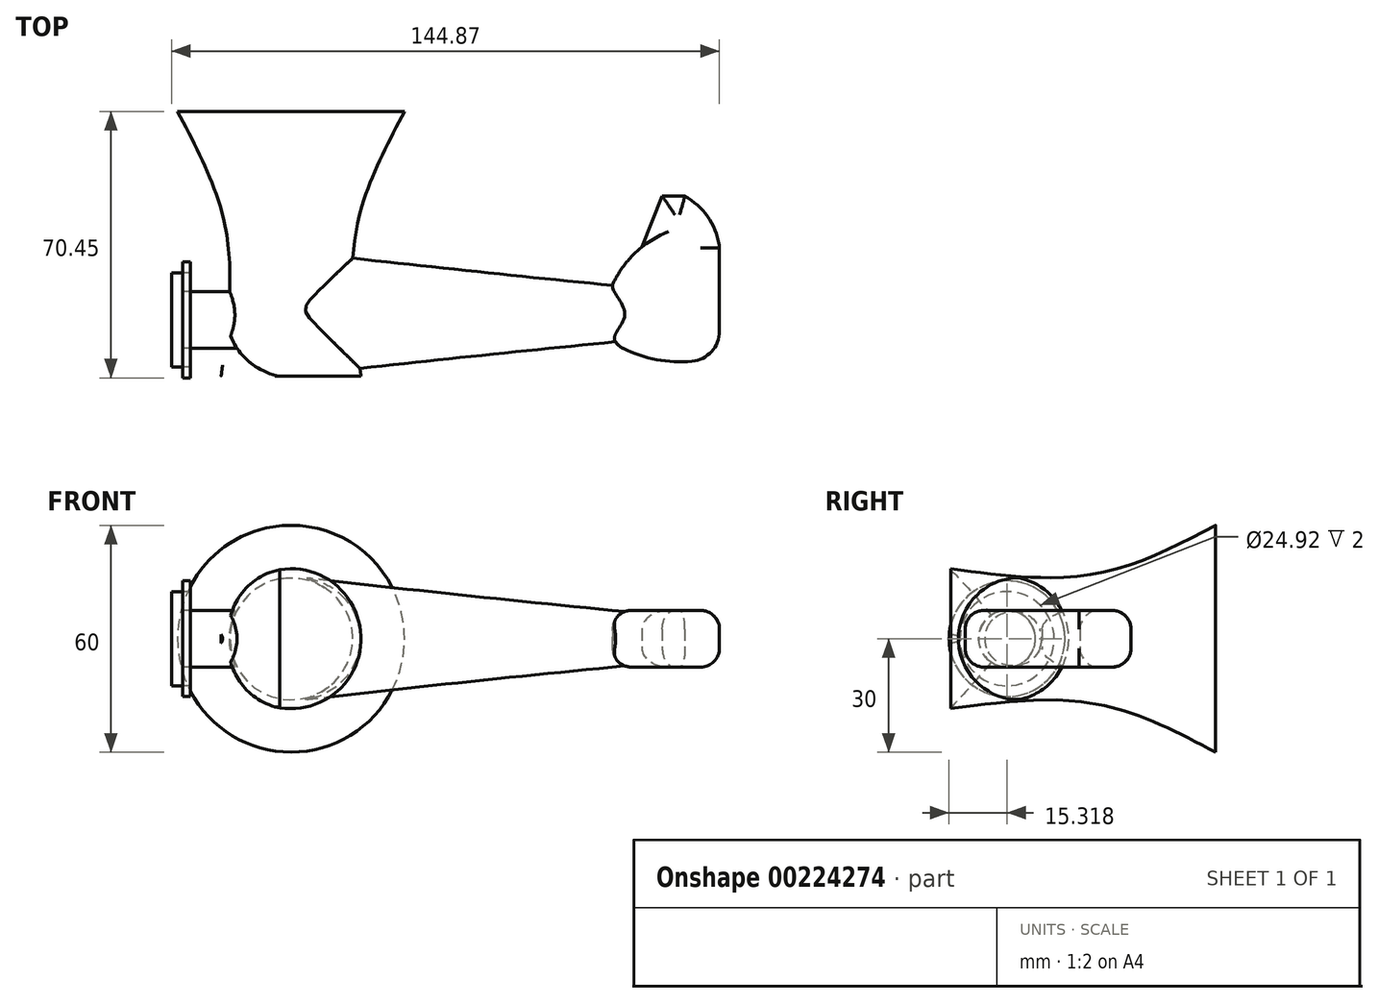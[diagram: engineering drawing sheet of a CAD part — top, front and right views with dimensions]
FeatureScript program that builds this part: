
annotation { "Feature Type Name" : "Feature", "Feature Type Description" : "" }
export const myFeature = defineFeature(function(context is Context, id is Id, definition is map)
    precondition{}
    {
        {
            var Q0;
            Q0=qCreatedBy(makeId("Front.planeOp"),FACE);
            var sketch = newSketch(context, id + "F0", { "sketchPlane" : qUnion([Q0])});
            skCircle(sketch, "E0", {"center": v(0, 0) * mm, "radius": 30 * mm});
            skSolve(sketch);
        }
        {
            var Q0;
            Q0=makeQuery(id+"F0.imprint","IMPRINT",FACE,{"disambiguationData":[TD([[makeQuery(id+"F0.imprint","IMPRINT",EDGE,{"derivedFrom":sQuery(id+"F0.wireOp",EDGE,"E0")}),1.0]])]});
            cPlane(context, id + "F1", {"entities" : qUnion([Q0]), "cplaneType" : CPlaneType.OFFSET, "offset" : 70 * mm, "width" : 150 * mm, "height" : 150 * mm});
        }
        {
            var Q0;
            Q0=qCreatedBy(id+"F1.planeOp",FACE);
            cPlane(context, id + "F2", {"entities" : qUnion([Q0]), "cplaneType" : CPlaneType.OFFSET, "offset" : 40 * mm, "oppositeDirection" : true, "width" : 150 * mm, "height" : 150 * mm});
        }
        {
            var Q0;
            Q0=qCreatedBy(id+"F2.planeOp",FACE);
            var sketch = newSketch(context, id + "F3", { "sketchPlane" : qUnion([Q0])});
            skCircle(sketch, "E1", {"center": v(0, 0) * mm, "radius": 17.5 * mm});
            skSolve(sketch);
        }
        {
            var Q0;
            Q0=qCreatedBy(id+"F1.planeOp",FACE);
            var sketch = newSketch(context, id + "F4", { "sketchPlane" : qUnion([Q0])});
            skCircle(sketch, "E2", {"center": v(0, 0) * mm, "radius": 18.5 * mm});
            skSolve(sketch);
        }
        {
            var Q0;
            Q0=makeQuery(id+"F4.imprint","IMPRINT",FACE,{"disambiguationData":[TD([[makeQuery(id+"F4.imprint","IMPRINT",EDGE,{"derivedFrom":sQuery(id+"F4.wireOp",EDGE,"E2")}),1.0]])]});
            var Q1;
            Q1=makeQuery(id+"F3.imprint","IMPRINT",FACE,{"disambiguationData":[TD([[makeQuery(id+"F3.imprint","IMPRINT",EDGE,{"derivedFrom":sQuery(id+"F3.wireOp",EDGE,"E1")}),1.0]])]});
            var Q2;
            Q2=makeQuery(id+"F0.imprint","IMPRINT",FACE,{"disambiguationData":[TD([[makeQuery(id+"F0.imprint","IMPRINT",EDGE,{"derivedFrom":sQuery(id+"F0.wireOp",EDGE,"E0")}),1.0]])]});
            loft(context, id + "F5", {"sheetProfilesArray" : [{ "sheetProfileEntities" : qUnion([Q0]) }, { "sheetProfileEntities" : qUnion([Q1]) }, { "sheetProfileEntities" : qUnion([Q2]) }]});
        }
        {
            var Q0;
            Q0=qCreatedBy(makeId("Right.planeOp"),FACE);
            cPlane(context, id + "F6", {"entities" : qUnion([Q0]), "cplaneType" : CPlaneType.OFFSET, "offset" : 60 * mm, "width" : 150 * mm, "height" : 150 * mm});
        }
        {
            var Q0;
            Q0=qCreatedBy(id+"F6.planeOp",FACE);
            cPlane(context, id + "F7", {"entities" : qUnion([Q0]), "cplaneType" : CPlaneType.OFFSET, "offset" : 25 * mm, "width" : 150 * mm, "height" : 150 * mm});
        }
        {
            var Q0;
            Q0=qCreatedBy(makeId("Right.planeOp"),FACE);
            var sketch = newSketch(context, id + "F8", { "sketchPlane" : qUnion([Q0])});
            skCircle(sketch, "E3", {"center": v(-53.5, 0) * mm, "radius": 16.5 * mm});
            skSolve(sketch);
        }
        {
            var Q0;
            Q0=qCreatedBy(id+"F6.planeOp",FACE);
            var sketch = newSketch(context, id + "F9", { "sketchPlane" : qUnion([Q0])});
            skCircle(sketch, "E4", {"center": v(-53.5, 0) * mm, "radius": 10 * mm});
            skSolve(sketch);
        }
        {
            var Q0;
            Q0=qCreatedBy(id+"F7.planeOp",FACE);
            var sketch = newSketch(context, id + "F10", { "sketchPlane" : qUnion([Q0])});
            skCircle(sketch, "E5", {"center": v(-53.5, 0) * mm, "radius": 7.5 * mm});
            skSolve(sketch);
        }
        {
            var Q1;
            Q1 = qSketchRegion(id + "F8", true);
            var Q2;
            Q2 = qSketchRegion(id + "F9", true);
            var Q3;
            Q3 = qSketchRegion(id + "F10", true);
            loft(context, id + "F11", {"operationType" : NewBodyOperationType.ADD, "sheetProfilesArray" : [{ "sheetProfileEntities" : qUnion([Q1]) }, { "sheetProfileEntities" : qUnion([Q2]) }, { "sheetProfileEntities" : qUnion([Q3]) }]});
        }
        {
            var Q0;
            Q0=qCreatedBy(makeId("Top.planeOp"),FACE);
            var sketch = newSketch(context, id + "F12", { "sketchPlane" : qUnion([Q0])});
            skArc(sketch, "E6", {"start": v(-2.52, -70.07) * mm, "mid": v(-11.8, -65.57) * mm, "end": v(-16.82, -56.57) * mm});
            skLineSegment(sketch, "E7", {"start": v(-2.52, -70.07) * mm, "end": v(-18.47, -70.07) * mm});
            skLineSegment(sketch, "E8", {"start": v(-18.47, -70.07) * mm, "end": v(-16.82, -56.57) * mm});
            skSolve(sketch);
        }
        {
            var Q0;
            Q0=qCreatedBy(makeId("Top.planeOp"),FACE);
            cPlane(context, id + "F13", {"entities" : qUnion([Q0]), "cplaneType" : CPlaneType.OFFSET, "offset" : 18 * mm, "oppositeDirection" : true, "width" : 150 * mm, "height" : 150 * mm});
        }
        {
            var Q0;
            Q0=qCreatedBy(makeId("Top.planeOp"),FACE);
            var sketch = newSketch(context, id + "F14", { "sketchPlane" : qUnion([Q0])});
            skArc(sketch, "E9.0", {"start": v(-2.52, -70.07) * mm, "mid": v(-11.8, -65.57) * mm, "end": v(-16.82, -56.57) * mm});
            skLineSegment(sketch, "E10.0", {"start": v(-2.52, -70.07) * mm, "end": v(-18.47, -70.07) * mm});
            skLineSegment(sketch, "E11.0", {"start": v(-18.47, -70.07) * mm, "end": v(-16.82, -56.57) * mm});
            skSolve(sketch);
        }
        {
            var Q0;
            Q0=qCreatedBy(id+"F13.planeOp",FACE);
            var sketch = newSketch(context, id + "F15", { "sketchPlane" : qUnion([Q0])});
            skArc(sketch, "E12.0", {"start": v(-2.52, -70.07) * mm, "mid": v(-11.8, -65.57) * mm, "end": v(-16.82, -56.57) * mm});
            skLineSegment(sketch, "E13.0", {"start": v(-2.52, -70.07) * mm, "end": v(-18.47, -70.07) * mm});
            skLineSegment(sketch, "E13.1", {"start": v(-18.47, -70.07) * mm, "end": v(-16.82, -56.57) * mm});
            skSolve(sketch);
        }
        {
            var Q0;
            Q0 = qSketchRegion(id + "F15", true);
            extrude(context, id + "F16", {"entities" : qUnion([Q0]), "operationType" : NewBodyOperationType.REMOVE, "endBound" : BoundingType.THROUGH_ALL, "depth" : 25 * mm});
        }
        {
            var Q0;
            Q0=qCreatedBy(makeId("Top.planeOp"),FACE);
            var sketch = newSketch(context, id + "F17", { "sketchPlane" : qUnion([Q0])});
            skLineSegment(sketch, "E14", {"start": v(113.26, -61.15) * mm, "end": v(113.26, -35.74) * mm});
            skLineSegment(sketch, "E15", {"start": v(98.14, -22.36) * mm, "end": v(92.74, -35.88) * mm});
            skArc(sketch, "E16", {"start": v(113.26, -64.6) * mm, "mid": v(98.75, -65.96) * mm, "end": v(85, -61.15) * mm});
            skLineSegment(sketch, "E17", {"start": v(113.26, -64.6) * mm, "end": v(113.26, -61.15) * mm});
            skArc(sketch, "E18", {"start": v(113.26, -35.74) * mm, "mid": v(110.25, -27.99) * mm, "end": v(104.12, -22.36) * mm});
            skLineSegment(sketch, "E19", {"start": v(98.14, -22.36) * mm, "end": v(104.12, -22.36) * mm});
            skArc(sketch, "E20", {"start": v(92.74, -35.88) * mm, "mid": v(88.28, -40.4) * mm, "end": v(85, -45.84) * mm});
            skLineSegment(sketch, "E21", {"start": v(85, -61.15) * mm, "end": v(85, -45.84) * mm});
            skSolve(sketch);
        }
        {
            var Q0;
            Q0 = qSketchRegion(id + "F17", true);
            extrude(context, id + "F18", {"entities" : qUnion([Q0]), "operationType" : NewBodyOperationType.ADD, "endBound" : BoundingType.SYMMETRIC, "depth" : 15 * mm});
        }
        {
            var Q0;
            Q0=makeQuery(id+"F18.opExtrude","SWEPT_EDGE",EDGE,{"disambiguationData":[OSD([sQuery(id+"F17.wireOp",EDGE,"E16"),sQuery(id+"F17.wireOp",EDGE,"E17")])]});
            fillet(context, id + "F19", {"entities" : qUnion([Q0]), "radius" : 8 * mm, "tangentPropagation" : true, "allowEdgeOverflow" : false});
        }
        {
            var Q0;
            {var subQ0=sQuery(id+"F17.wireOp",EDGE,"E21");var subQ1=sQuery(id+"F17.wireOp",EDGE,"E16");Q0=makeQuery(id+"F18.boolean.opBoolean","SPLIT",EDGE,{"disambiguationData":[TD([makeQuery(id+"F18.opExtrude","SWEPT_FACE",FACE,{"disambiguationData":[OSD([subQ1])]})])],"derivedFrom":makeQuery(id+"F18.opExtrude","CAP_EDGE",EDGE,{"disambiguationData":[OSD([subQ0])],"isStart":true})});}
            var Q1;
            {var subQ0=sQuery(id+"F17.wireOp",EDGE,"E21");var subQ1=sQuery(id+"F17.wireOp",EDGE,"E20");Q1=makeQuery(id+"F18.boolean.opBoolean","SPLIT",EDGE,{"disambiguationData":[TD([makeQuery(id+"F18.opExtrude","SWEPT_FACE",FACE,{"disambiguationData":[OSD([subQ1])]})])],"derivedFrom":makeQuery(id+"F18.opExtrude","CAP_EDGE",EDGE,{"disambiguationData":[OSD([subQ0])],"isStart":true})});}
            var Q2;
            Q2=makeQuery(id+"F18.opExtrude","SWEPT_EDGE",EDGE,{"disambiguationData":[OSD([sQuery(id+"F17.wireOp",EDGE,"E16"),sQuery(id+"F17.wireOp",EDGE,"E21")])]});
            fillet(context, id + "F20", {"entities" : qUnion([Q0, Q1, Q2]), "radius" : 5 * mm, "tangentPropagation" : true, "allowEdgeOverflow" : false});
        }
        {
            var Q0;
            Q0=makeQuery(id+"F18.opExtrude","CAP_EDGE",EDGE,{"disambiguationData":[OSD([sQuery(id+"F17.wireOp",EDGE,"E16")])],"isStart":true});
            fillet(context, id + "F21", {"entities" : qUnion([Q0]), "radius" : 5 * mm, "tangentPropagation" : true, "allowEdgeOverflow" : false});
        }
        {
            var Q0;
            Q0=makeQuery(id+"F18.opExtrude","CAP_EDGE",EDGE,{"disambiguationData":[OSD([sQuery(id+"F17.wireOp",EDGE,"E16")])],"isStart":false});
            var Q1;
            {var subQ0=sQuery(id+"F17.wireOp",EDGE,"E21");var subQ1=sQuery(id+"F17.wireOp",EDGE,"E20");Q1=makeQuery(id+"F18.boolean.opBoolean","SPLIT",EDGE,{"disambiguationData":[TD([makeQuery(id+"F18.opExtrude","SWEPT_FACE",FACE,{"disambiguationData":[OSD([subQ1])]})])],"derivedFrom":makeQuery(id+"F18.opExtrude","CAP_EDGE",EDGE,{"disambiguationData":[OSD([subQ0])],"isStart":false})});}
            var Q2;
            Q2=makeQuery(id+"F18.opExtrude","CAP_EDGE",EDGE,{"disambiguationData":[OSD([sQuery(id+"F17.wireOp",EDGE,"E15")])],"isStart":false});
            var Q3;
            Q3=makeQuery(id+"F18.opExtrude","CAP_EDGE",EDGE,{"disambiguationData":[OSD([sQuery(id+"F17.wireOp",EDGE,"E19")])],"isStart":false});
            fillet(context, id + "F22", {"entities" : qUnion([Q0, Q1, Q2, Q3]), "radius" : 5 * mm, "tangentPropagation" : true, "allowEdgeOverflow" : false});
        }
        {
            var Q0;
            Q0=makeQuery(id+"F18.opExtrude","CAP_EDGE",EDGE,{"disambiguationData":[OSD([sQuery(id+"F17.wireOp",EDGE,"E19")])],"isStart":true});
            var Q1;
            Q1=makeQuery(id+"F18.opExtrude","CAP_EDGE",EDGE,{"disambiguationData":[OSD([sQuery(id+"F17.wireOp",EDGE,"E18")])],"isStart":true});
            var Q2;
            Q2=makeQuery(id+"F21.opFillet","BLEND_EDGE",EDGE,{"blendedFrom":[makeQuery(id+"F18.opExtrude","CAP_EDGE",EDGE,{"disambiguationData":[OSD([sQuery(id+"F17.wireOp",EDGE,"E14"),sQuery(id+"F17.wireOp",EDGE,"E17")])],"isStart":true}),makeQuery(id+"F18.opExtrude","SWEPT_FACE",FACE,{"disambiguationData":[OSD([sQuery(id+"F17.wireOp",EDGE,"E18")])]})],"blendedInto":[makeQuery(id+"F18.opExtrude","SWEPT_FACE",FACE,{"disambiguationData":[OSD([sQuery(id+"F17.wireOp",EDGE,"E18")])]})]});
            var Q3;
            Q3=makeQuery(id+"F18.opExtrude","CAP_EDGE",EDGE,{"disambiguationData":[OSD([sQuery(id+"F17.wireOp",EDGE,"E15")])],"isStart":true});
            fillet(context, id + "F23", {"entities" : qUnion([Q0, Q1, Q2, Q3]), "radius" : 5 * mm, "tangentPropagation" : true, "allowEdgeOverflow" : false});
        }
        {
            var Q0;
            Q0=qCreatedBy(makeId("Top.planeOp"),FACE);
            var sketch = newSketch(context, id + "F24", { "sketchPlane" : qUnion([Q0])});
            skLineSegment(sketch, "E22", {"start": v(-13.96, -62.63) * mm, "end": v(-28.6, -62.63) * mm});
            skLineSegment(sketch, "E23", {"start": v(-28.6, -62.63) * mm, "end": v(-28.6, -47.64) * mm});
            skLineSegment(sketch, "E24", {"start": v(-28.6, -47.64) * mm, "end": v(-13.96, -47.64) * mm});
            skLineSegment(sketch, "E25", {"start": v(-13.96, -47.64) * mm, "end": v(-13.96, -62.63) * mm});
            skLineSegment(sketch, "E26", {"start": v(-28.6, -55.13) * mm, "end": v(-13.96, -55.13) * mm});
            skSolve(sketch);
        }
        {
            var Q0;
            {var subQ0=sQuery(id+"F24.wireOp",EDGE,"E22");Q0=makeQuery(id+"F24.imprint","IMPRINT",FACE,{"disambiguationData":[TD([[makeQuery(id+"F24.imprint","IMPRINT",EDGE,{"derivedFrom":subQ0}),-1.0]])]});}
            var Q1;
            Q1=sQuery(id+"F24.wireOp",EDGE,"E26");
            revolve(context, id + "F25", {"operationType" : NewBodyOperationType.ADD, "entities" : qUnion([Q0]), "axis" : qUnion([Q1]), "revolveType" : RevolveType.FULL});
        }
        {
            var Q0;
            Q0=makeQuery(id+"F25.opRevolve","SWEPT_FACE",FACE,{"disambiguationData":[OSD([sQuery(id+"F24.wireOp",EDGE,"E23")])]});
            var sketch = newSketch(context, id + "F26", { "sketchPlane" : qUnion([Q0])});
            skCircle(sketch, "E27", {"center": v(55.13, 0) * mm, "radius": 15.32 * mm});
            skCircle(sketch, "E28", {"center": v(55.13, 0) * mm, "radius": 12.46 * mm});
            skSolve(sketch);
        }
        {
            var Q0;
            Q0=makeQuery(id+"F26.imprint","IMPRINT",FACE,{"disambiguationData":[TD([[makeQuery(id+"F26.imprint","IMPRINT",EDGE,{"derivedFrom":sQuery(id+"F26.wireOp",EDGE,"E28")}),1.0]])]});
            extrude(context, id + "F27", {"entities" : qUnion([Q0]), "depth" : 3 * mm});
        }
        {
            var Q0;
            Q0=makeQuery(id+"F26.imprint","IMPRINT",FACE,{"disambiguationData":[TD([[makeQuery(id+"F26.imprint","IMPRINT",EDGE,{"derivedFrom":sQuery(id+"F26.wireOp",EDGE,"E27")}),1.0]])]});
            extrude(context, id + "F28", {"entities" : qUnion([Q0]), "oppositeDirection" : true, "depth" : 2 * mm});
        }
        {
            var Q0;
            Q0=makeQuery(id+"F26.imprint","IMPRINT",FACE,{"disambiguationData":[TD([[makeQuery(id+"F26.imprint","IMPRINT",EDGE,{"derivedFrom":makeQuery(id+"F25.opRevolve","SWEPT_EDGE",EDGE,{"disambiguationData":[OSD([sQuery(id+"F24.wireOp",EDGE,"E22"),sQuery(id+"F24.wireOp",EDGE,"E23")])]})}),1.0]])]});
            extrude(context, id + "F29", {"entities" : qUnion([Q0]), "operationType" : NewBodyOperationType.ADD, "depth" : 3 * mm});
        }
    });
